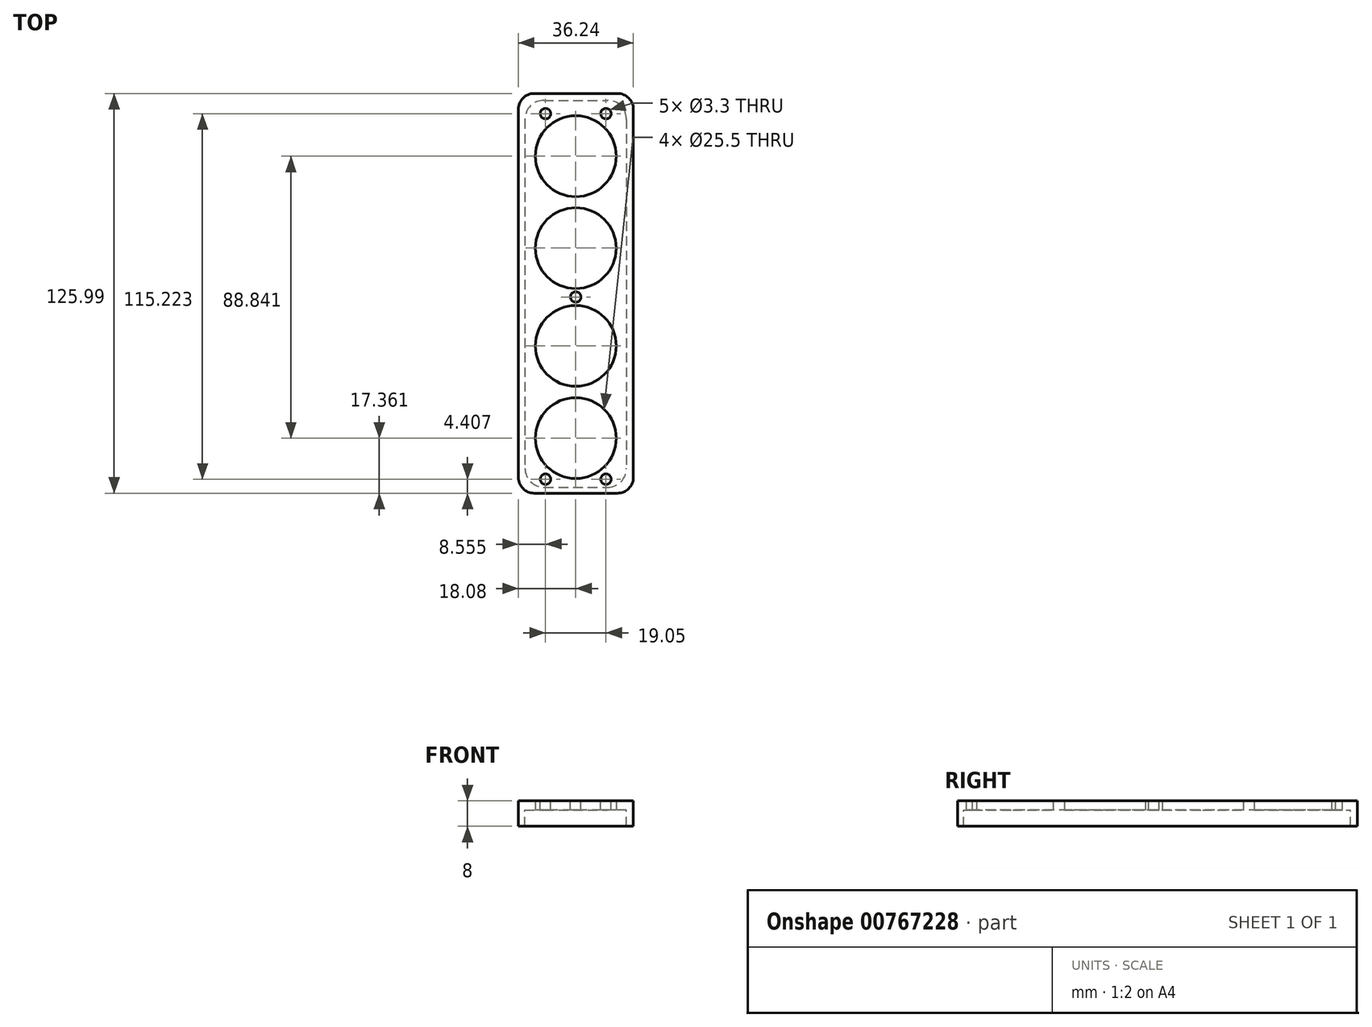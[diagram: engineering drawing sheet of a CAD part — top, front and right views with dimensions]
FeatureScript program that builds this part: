
annotation { "Feature Type Name" : "Feature", "Feature Type Description" : "" }
export const myFeature = defineFeature(function(context is Context, id is Id, definition is map)
    precondition{}
    {
        {
            var Q0;
            Q0=qCreatedBy(makeId("Top.planeOp"),FACE);
            var sketch = newSketch(context, id + "F0", { "sketchPlane" : qUnion([Q0])});
            skLineSegment(sketch, "E0.bottom", {"start": v(-16, 61.99) * mm, "end": v(16, 61.99) * mm});
            skLineSegment(sketch, "E0.top", {"start": v(-16, -60.01) * mm, "end": v(16, -60.01) * mm});
            skLineSegment(sketch, "E0.left", {"start": v(-16, 61.99) * mm, "end": v(-16, -60.01) * mm});
            skLineSegment(sketch, "E0.right", {"start": v(16, 61.99) * mm, "end": v(16, -60.01) * mm});
            skCircle(sketch, "E1", {"center": v(0, 44.36) * mm, "radius": 12.75 * mm});
            skCircle(sketch, "E2", {"center": v(0, 15.4) * mm, "radius": 12.75 * mm});
            skCircle(sketch, "E3", {"center": v(0, -15.42) * mm, "radius": 12.75 * mm});
            skCircle(sketch, "E4", {"center": v(0, -44.48) * mm, "radius": 12.75 * mm});
            skLineSegment(sketch, "E5", {"start": v(9.53, 68.25) * mm, "end": v(9.53, -73.05) * mm, "construction": true});
            skLineSegment(sketch, "E6", {"start": v(-9.53, 68.25) * mm, "end": v(-9.53, -73.05) * mm, "construction": true});
            skCircle(sketch, "E7", {"center": v(-9.53, 44.36) * mm, "radius": 1 * mm});
            skCircle(sketch, "E8", {"center": v(9.53, 44.36) * mm, "radius": 1 * mm});
            skCircle(sketch, "E9", {"center": v(9.53, 44.36) * mm, "radius": 2 * mm});
            skCircle(sketch, "E10", {"center": v(-9.53, 44.36) * mm, "radius": 2 * mm});
            skCircle(sketch, "E11", {"center": v(9.53, 15.4) * mm, "radius": 1 * mm});
            skCircle(sketch, "E12", {"center": v(9.53, 15.4) * mm, "radius": 2 * mm});
            skCircle(sketch, "E13", {"center": v(-9.53, 15.4) * mm, "radius": 1 * mm});
            skCircle(sketch, "E14", {"center": v(-9.53, 15.4) * mm, "radius": 2 * mm});
            skCircle(sketch, "E15", {"center": v(9.53, -15.42) * mm, "radius": 1 * mm});
            skCircle(sketch, "E16", {"center": v(9.53, -15.42) * mm, "radius": 2 * mm});
            skCircle(sketch, "E17", {"center": v(-9.53, -15.42) * mm, "radius": 1 * mm});
            skCircle(sketch, "E18", {"center": v(-9.53, -15.42) * mm, "radius": 2 * mm});
            skCircle(sketch, "E19", {"center": v(9.53, -44.48) * mm, "radius": 1 * mm});
            skCircle(sketch, "E20", {"center": v(9.53, -44.48) * mm, "radius": 2 * mm});
            skCircle(sketch, "E21", {"center": v(-9.53, -44.48) * mm, "radius": 1 * mm});
            skCircle(sketch, "E22", {"center": v(-9.53, -44.48) * mm, "radius": 2 * mm});
            skCircle(sketch, "E23", {"center": v(9.53, 57.8) * mm, "radius": 1.65 * mm});
            skCircle(sketch, "E24", {"center": v(-9.53, 57.8) * mm, "radius": 1.65 * mm});
            skCircle(sketch, "E25", {"center": v(9.53, 29.2) * mm, "radius": 1.25 * mm});
            skCircle(sketch, "E26", {"center": v(-9.53, 29.2) * mm, "radius": 1.25 * mm});
            skCircle(sketch, "E27", {"center": v(9.53, 0) * mm, "radius": 1.25 * mm});
            skCircle(sketch, "E28", {"center": v(-9.53, 0) * mm, "radius": 1.25 * mm});
            skCircle(sketch, "E29", {"center": v(9.53, -30.47) * mm, "radius": 1.25 * mm});
            skCircle(sketch, "E30", {"center": v(-9.53, -30.47) * mm, "radius": 1.25 * mm});
            skCircle(sketch, "E31", {"center": v(9.53, -57.43) * mm, "radius": 1.65 * mm});
            skCircle(sketch, "E32", {"center": v(-9.53, -57.43) * mm, "radius": 1.65 * mm});
            skCircle(sketch, "E33", {"center": v(0, 0) * mm, "radius": 1.65 * mm});
            skLineSegment(sketch, "E34.bottom", {"start": v(-18.08, 64.15) * mm, "end": v(18.16, 64.15) * mm});
            skLineSegment(sketch, "E34.top", {"start": v(-18.08, -61.84) * mm, "end": v(18.16, -61.84) * mm});
            skLineSegment(sketch, "E34.left", {"start": v(-18.08, 64.15) * mm, "end": v(-18.08, -61.84) * mm});
            skLineSegment(sketch, "E34.right", {"start": v(18.16, 64.15) * mm, "end": v(18.16, -61.84) * mm});
            skSolve(sketch);
        }
        {
            var Q0;
            Q0=makeQuery(id+"F0.imprint","IMPRINT",FACE,{"disambiguationData":[TD([[makeQuery(id+"F0.imprint","IMPRINT",EDGE,{"derivedFrom":sQuery(id+"F0.wireOp",EDGE,"E1")}),-1.0]])]});
            var Q1;
            Q1=makeQuery(id+"F0.imprint","IMPRINT",FACE,{"disambiguationData":[TD([[makeQuery(id+"F0.imprint","IMPRINT",EDGE,{"derivedFrom":sQuery(id+"F0.wireOp",EDGE,"E27")}),1.0]])]});
            var Q2;
            Q2=makeQuery(id+"F0.imprint","IMPRINT",FACE,{"disambiguationData":[TD([[makeQuery(id+"F0.imprint","IMPRINT",EDGE,{"derivedFrom":sQuery(id+"F0.wireOp",EDGE,"E28")}),1.0]])]});
            var Q3;
            Q3=makeQuery(id+"F0.imprint","IMPRINT",FACE,{"disambiguationData":[TD([[makeQuery(id+"F0.imprint","IMPRINT",EDGE,{"derivedFrom":sQuery(id+"F0.wireOp",EDGE,"E25")}),1.0]])]});
            var Q4;
            Q4=makeQuery(id+"F0.imprint","IMPRINT",FACE,{"disambiguationData":[TD([[makeQuery(id+"F0.imprint","IMPRINT",EDGE,{"derivedFrom":sQuery(id+"F0.wireOp",EDGE,"E26")}),1.0]])]});
            var Q5;
            Q5=makeQuery(id+"F0.imprint","IMPRINT",FACE,{"disambiguationData":[TD([[makeQuery(id+"F0.imprint","IMPRINT",EDGE,{"derivedFrom":sQuery(id+"F0.wireOp",EDGE,"E29")}),1.0]])]});
            var Q6;
            Q6=makeQuery(id+"F0.imprint","IMPRINT",FACE,{"disambiguationData":[TD([[makeQuery(id+"F0.imprint","IMPRINT",EDGE,{"derivedFrom":sQuery(id+"F0.wireOp",EDGE,"E30")}),1.0]])]});
            var Q7;
            Q7=makeQuery(id+"F0.imprint","IMPRINT",FACE,{"disambiguationData":[TD([[makeQuery(id+"F0.imprint","IMPRINT",EDGE,{"derivedFrom":sQuery(id+"F0.wireOp",EDGE,"E31")}),1.0]])]});
            var Q8;
            Q8=makeQuery(id+"F0.imprint","IMPRINT",FACE,{"disambiguationData":[TD([[makeQuery(id+"F0.imprint","IMPRINT",EDGE,{"derivedFrom":sQuery(id+"F0.wireOp",EDGE,"E32")}),1.0]])]});
            var Q9;
            Q9=makeQuery(id+"F0.imprint","IMPRINT",FACE,{"disambiguationData":[TD([[makeQuery(id+"F0.imprint","IMPRINT",EDGE,{"derivedFrom":sQuery(id+"F0.wireOp",EDGE,"E33")}),1.0]])]});
            var Q10;
            Q10=makeQuery(id+"F0.imprint","IMPRINT",FACE,{"disambiguationData":[TD([[makeQuery(id+"F0.imprint","IMPRINT",EDGE,{"derivedFrom":sQuery(id+"F0.wireOp",EDGE,"E23")}),1.0]])]});
            var Q11;
            Q11=makeQuery(id+"F0.imprint","IMPRINT",FACE,{"disambiguationData":[TD([[makeQuery(id+"F0.imprint","IMPRINT",EDGE,{"derivedFrom":sQuery(id+"F0.wireOp",EDGE,"E24")}),1.0]])]});
            extrude(context, id + "F1", {"entities" : qUnion([Q0, Q1, Q2, Q3, Q4, Q5, Q6, Q7, Q8, Q9, Q10, Q11]), "depth" : 6 * mm, "offsetDistance" : 25 * mm, "hasSecondDirection" : true, "secondDirectionOppositeDirection" : false, "secondDirectionDepth" : 3.1 * mm});
        }
        {
            var Q0;
            Q0=makeQuery(id+"F0.imprint","IMPRINT",FACE,{"disambiguationData":[TD([[makeQuery(id+"F0.imprint","IMPRINT",EDGE,{"derivedFrom":sQuery(id+"F0.wireOp",EDGE,"E1")}),1.0]])]});
            var Q1;
            Q1=makeQuery(id+"F0.imprint","IMPRINT",FACE,{"disambiguationData":[TD([[makeQuery(id+"F0.imprint","IMPRINT",EDGE,{"derivedFrom":sQuery(id+"F0.wireOp",EDGE,"E2")}),1.0]])]});
            var Q2;
            Q2=makeQuery(id+"F0.imprint","IMPRINT",FACE,{"disambiguationData":[TD([[makeQuery(id+"F0.imprint","IMPRINT",EDGE,{"derivedFrom":sQuery(id+"F0.wireOp",EDGE,"E3")}),1.0]])]});
            var Q3;
            Q3=makeQuery(id+"F0.imprint","IMPRINT",FACE,{"disambiguationData":[TD([[makeQuery(id+"F0.imprint","IMPRINT",EDGE,{"derivedFrom":sQuery(id+"F0.wireOp",EDGE,"E4")}),1.0]])]});
            var Q4;
            Q4=makeQuery(id+"F0.imprint","IMPRINT",FACE,{"disambiguationData":[TD([[makeQuery(id+"F0.imprint","IMPRINT",EDGE,{"derivedFrom":sQuery(id+"F0.wireOp",EDGE,"E8")}),1.0]])]});
            var Q5;
            Q5=makeQuery(id+"F0.imprint","IMPRINT",FACE,{"disambiguationData":[TD([[makeQuery(id+"F0.imprint","IMPRINT",EDGE,{"derivedFrom":sQuery(id+"F0.wireOp",EDGE,"E8")}),-1.0]])]});
            var Q6;
            Q6=makeQuery(id+"F0.imprint","IMPRINT",FACE,{"disambiguationData":[TD([[makeQuery(id+"F0.imprint","IMPRINT",EDGE,{"derivedFrom":sQuery(id+"F0.wireOp",EDGE,"E7")}),1.0]])]});
            var Q7;
            Q7=makeQuery(id+"F0.imprint","IMPRINT",FACE,{"disambiguationData":[TD([[makeQuery(id+"F0.imprint","IMPRINT",EDGE,{"derivedFrom":sQuery(id+"F0.wireOp",EDGE,"E7")}),-1.0]])]});
            var Q8;
            Q8=makeQuery(id+"F0.imprint","IMPRINT",FACE,{"disambiguationData":[TD([[makeQuery(id+"F0.imprint","IMPRINT",EDGE,{"derivedFrom":sQuery(id+"F0.wireOp",EDGE,"E11")}),1.0]])]});
            var Q9;
            Q9=makeQuery(id+"F0.imprint","IMPRINT",FACE,{"disambiguationData":[TD([[makeQuery(id+"F0.imprint","IMPRINT",EDGE,{"derivedFrom":sQuery(id+"F0.wireOp",EDGE,"E11")}),-1.0]])]});
            var Q10;
            Q10=makeQuery(id+"F0.imprint","IMPRINT",FACE,{"disambiguationData":[TD([[makeQuery(id+"F0.imprint","IMPRINT",EDGE,{"derivedFrom":sQuery(id+"F0.wireOp",EDGE,"E13")}),1.0]])]});
            var Q11;
            Q11=makeQuery(id+"F0.imprint","IMPRINT",FACE,{"disambiguationData":[TD([[makeQuery(id+"F0.imprint","IMPRINT",EDGE,{"derivedFrom":sQuery(id+"F0.wireOp",EDGE,"E13")}),-1.0]])]});
            var Q12;
            Q12=makeQuery(id+"F0.imprint","IMPRINT",FACE,{"disambiguationData":[TD([[makeQuery(id+"F0.imprint","IMPRINT",EDGE,{"derivedFrom":sQuery(id+"F0.wireOp",EDGE,"E15")}),1.0]])]});
            var Q13;
            Q13=makeQuery(id+"F0.imprint","IMPRINT",FACE,{"disambiguationData":[TD([[makeQuery(id+"F0.imprint","IMPRINT",EDGE,{"derivedFrom":sQuery(id+"F0.wireOp",EDGE,"E15")}),-1.0]])]});
            var Q14;
            Q14=makeQuery(id+"F0.imprint","IMPRINT",FACE,{"disambiguationData":[TD([[makeQuery(id+"F0.imprint","IMPRINT",EDGE,{"derivedFrom":sQuery(id+"F0.wireOp",EDGE,"E17")}),1.0]])]});
            var Q15;
            Q15=makeQuery(id+"F0.imprint","IMPRINT",FACE,{"disambiguationData":[TD([[makeQuery(id+"F0.imprint","IMPRINT",EDGE,{"derivedFrom":sQuery(id+"F0.wireOp",EDGE,"E17")}),-1.0]])]});
            var Q16;
            Q16=makeQuery(id+"F0.imprint","IMPRINT",FACE,{"disambiguationData":[TD([[makeQuery(id+"F0.imprint","IMPRINT",EDGE,{"derivedFrom":sQuery(id+"F0.wireOp",EDGE,"E19")}),1.0]])]});
            var Q17;
            Q17=makeQuery(id+"F0.imprint","IMPRINT",FACE,{"disambiguationData":[TD([[makeQuery(id+"F0.imprint","IMPRINT",EDGE,{"derivedFrom":sQuery(id+"F0.wireOp",EDGE,"E19")}),-1.0]])]});
            var Q18;
            Q18=makeQuery(id+"F0.imprint","IMPRINT",FACE,{"disambiguationData":[TD([[makeQuery(id+"F0.imprint","IMPRINT",EDGE,{"derivedFrom":sQuery(id+"F0.wireOp",EDGE,"E21")}),-1.0]])]});
            var Q19;
            Q19=makeQuery(id+"F0.imprint","IMPRINT",FACE,{"disambiguationData":[TD([[makeQuery(id+"F0.imprint","IMPRINT",EDGE,{"derivedFrom":sQuery(id+"F0.wireOp",EDGE,"E21")}),1.0]])]});
            extrude(context, id + "F2", {"entities" : qUnion([Q0, Q1, Q2, Q3, Q4, Q5, Q6, Q7, Q8, Q9, Q10, Q11, Q12, Q13, Q14, Q15, Q16, Q17, Q18, Q19]), "operationType" : NewBodyOperationType.REMOVE, "depth" : 5 * mm, "offsetDistance" : 25 * mm, "hasSecondDirection" : true, "secondDirectionOppositeDirection" : false, "secondDirectionDepth" : 3 * mm});
        }
        {
            var Q0;
            Q0=makeQuery(id+"F0.imprint","IMPRINT",FACE,{"disambiguationData":[TD([[makeQuery(id+"F0.imprint","IMPRINT",EDGE,{"derivedFrom":sQuery(id+"F0.wireOp",EDGE,"E31")}),1.0]])]});
            var Q1;
            Q1=makeQuery(id+"F0.imprint","IMPRINT",FACE,{"disambiguationData":[TD([[makeQuery(id+"F0.imprint","IMPRINT",EDGE,{"derivedFrom":sQuery(id+"F0.wireOp",EDGE,"E33")}),1.0]])]});
            var Q2;
            Q2=makeQuery(id+"F0.imprint","IMPRINT",FACE,{"disambiguationData":[TD([[makeQuery(id+"F0.imprint","IMPRINT",EDGE,{"derivedFrom":sQuery(id+"F0.wireOp",EDGE,"E32")}),1.0]])]});
            var Q3;
            Q3=makeQuery(id+"F0.imprint","IMPRINT",FACE,{"disambiguationData":[TD([[makeQuery(id+"F0.imprint","IMPRINT",EDGE,{"derivedFrom":sQuery(id+"F0.wireOp",EDGE,"E24")}),1.0]])]});
            var Q4;
            Q4=makeQuery(id+"F0.imprint","IMPRINT",FACE,{"disambiguationData":[TD([[makeQuery(id+"F0.imprint","IMPRINT",EDGE,{"derivedFrom":sQuery(id+"F0.wireOp",EDGE,"E23")}),1.0]])]});
            extrude(context, id + "F3", {"entities" : qUnion([Q0, Q1, Q2, Q3, Q4]), "operationType" : NewBodyOperationType.REMOVE, "oppositeDirection" : true, "depth" : 25 * mm, "offsetDistance" : 25 * mm, "hasSecondDirection" : true, "secondDirectionOppositeDirection" : false, "secondDirectionDepth" : 39.8 * mm});
        }
        {
            var Q0;
            Q0=makeQuery(id+"F0.imprint","IMPRINT",FACE,{"disambiguationData":[TD([[makeQuery(id+"F0.imprint","IMPRINT",EDGE,{"derivedFrom":sQuery(id+"F0.wireOp",EDGE,"YlCcsRXM-vPrj-fovj-Ikgm-niUyzEBcnUbJ.bottom")}),-1.0]])]});
            var Q1;
            Q1=makeQuery(id+"F0.imprint","IMPRINT",FACE,{"disambiguationData":[TD([[makeQuery(id+"F0.imprint","IMPRINT",EDGE,{"derivedFrom":sQuery(id+"F0.wireOp",EDGE,"E0.bottom")}),1.0]])]});
            extrude(context, id + "F4", {"entities" : qUnion([Q0, Q1]), "operationType" : NewBodyOperationType.ADD, "oppositeDirection" : true, "depth" : 2 * mm, "offsetDistance" : 25 * mm, "hasSecondDirection" : true, "secondDirectionOppositeDirection" : false, "secondDirectionDepth" : 6 * mm});
        }
        {
            var Q0;
            Q0=makeQuery(id+"F4.opExtrude","SWEPT_EDGE",EDGE,{"disambiguationData":[OSD([sQuery(id+"F0.wireOp",EDGE,"E0.top"),sQuery(id+"F0.wireOp",EDGE,"E0.left")])]});
            var Q1;
            Q1=makeQuery(id+"F4.opExtrude","SWEPT_EDGE",EDGE,{"disambiguationData":[OSD([sQuery(id+"F0.wireOp",EDGE,"E0.top"),sQuery(id+"F0.wireOp",EDGE,"E0.right")])]});
            var Q2;
            Q2=makeQuery(id+"F4.opExtrude","SWEPT_EDGE",EDGE,{"disambiguationData":[OSD([sQuery(id+"F0.wireOp",EDGE,"E0.bottom"),sQuery(id+"F0.wireOp",EDGE,"E0.left")])]});
            var Q3;
            Q3=makeQuery(id+"F4.opExtrude","SWEPT_EDGE",EDGE,{"disambiguationData":[OSD([sQuery(id+"F0.wireOp",EDGE,"E0.bottom"),sQuery(id+"F0.wireOp",EDGE,"E0.right")])]});
            fillet(context, id + "F5", {"entities" : qUnion([Q0, Q1, Q2, Q3]), "radius" : 6 * mm, "tangentPropagation" : true, "allowEdgeOverflow" : false});
        }
        {
            var Q0;
            Q0=makeQuery(id+"F4.opExtrude","SWEPT_EDGE",EDGE,{"disambiguationData":[OSD([sQuery(id+"F0.wireOp",EDGE,"E34.bottom"),sQuery(id+"F0.wireOp",EDGE,"E34.right")])]});
            var Q1;
            Q1=makeQuery(id+"F4.opExtrude","SWEPT_EDGE",EDGE,{"disambiguationData":[OSD([sQuery(id+"F0.wireOp",EDGE,"E34.bottom"),sQuery(id+"F0.wireOp",EDGE,"E34.left")])]});
            var Q2;
            Q2=makeQuery(id+"F4.opExtrude","SWEPT_EDGE",EDGE,{"disambiguationData":[OSD([sQuery(id+"F0.wireOp",EDGE,"E34.top"),sQuery(id+"F0.wireOp",EDGE,"E34.left")])]});
            var Q3;
            Q3=makeQuery(id+"F4.opExtrude","SWEPT_EDGE",EDGE,{"disambiguationData":[OSD([sQuery(id+"F0.wireOp",EDGE,"E34.top"),sQuery(id+"F0.wireOp",EDGE,"E34.right")])]});
            fillet(context, id + "F6", {"entities" : qUnion([Q0, Q1, Q2, Q3]), "tangentPropagation" : true, "radius" : 5 * mm, "defaultsChanged" : false, "vertexSettings" : [], "allowEdgeOverflow" : false});
        }
    });
